# Revit family: TSM Betonschraube Innengewindemuffe SW13, vz
name_source: partatom
category: HLS-Bauteile
units: mm (PartAtom-declared; Revit-internal decimal feet)

## family parameters
Arbeitsebenenbasiert = Ja
Beim Laden mit Abzugskörper schneiden = Nein
Bemaßung runder Anschluss = Durchmesser verwenden
Beschriftungsausrichtung beibehalten = Nein
Gemeinsam genutzt = Ja
Immer vertikal = Nein
Raumberechnungspunkt = Nein
Teiletyp = Normal

## types (2) — shared parameters
Bohrerdurchmesser = 6 mm
Fabrikat = Toge
Firma = MEFA Befestigungs- und Montagesysteme GmbH
Form Kopf = Muffe
Innengewinde = M8/M10
Kurztext1 = Betonschraube TSM
Material = Stahl
Mengeneinheit = St
Oberflaeche = galvanisch verzinkt
Schlüsselweite = 13
Vorgabe-Ansicht = 1219 mm
vpe = 50
zero-valued in all types: max. Klemmstärke

## per-type parameters (varying)
| type | Artikelnummer | Durchmesser Kopf | EAN | Gewicht | Gewicht pro Bauteil | Innengewindemuffe | Kurztext2 | Länge | min. Bohrlochtiefe | min. Verankerungstiefe |
| TSM  Innengewindemuffe, SW13, verzinkt  6x 35 M 8/M10 | 2230000 | 16 mm | 4250928449825 | 0.03 kg | 0.03 kg | Innengewindemuffe, vz  6x 35 Muffe M 8 | 6x35 mm Muffe M8/M10 | 35 mm  [stored 0.114829 ft] | 40 mm | 35 mm |
| TSM  Innengewindemuffe, SW13, verzinkt  6x 55 M 8/M10 | 2230001 |  | 4260116911454 | 0.04 kg | 0.04 kg | Innengewindemuffe, vz  6x 55 Muffe M 8 | 6x55 mm Muffe M8/M10 | 55 mm  [stored 0.180446 ft] | 60 mm | 55 mm |

note: [stored X ft] marks values corroborated as IEEE doubles in the binary element streams (Revit-internal decimal feet)
